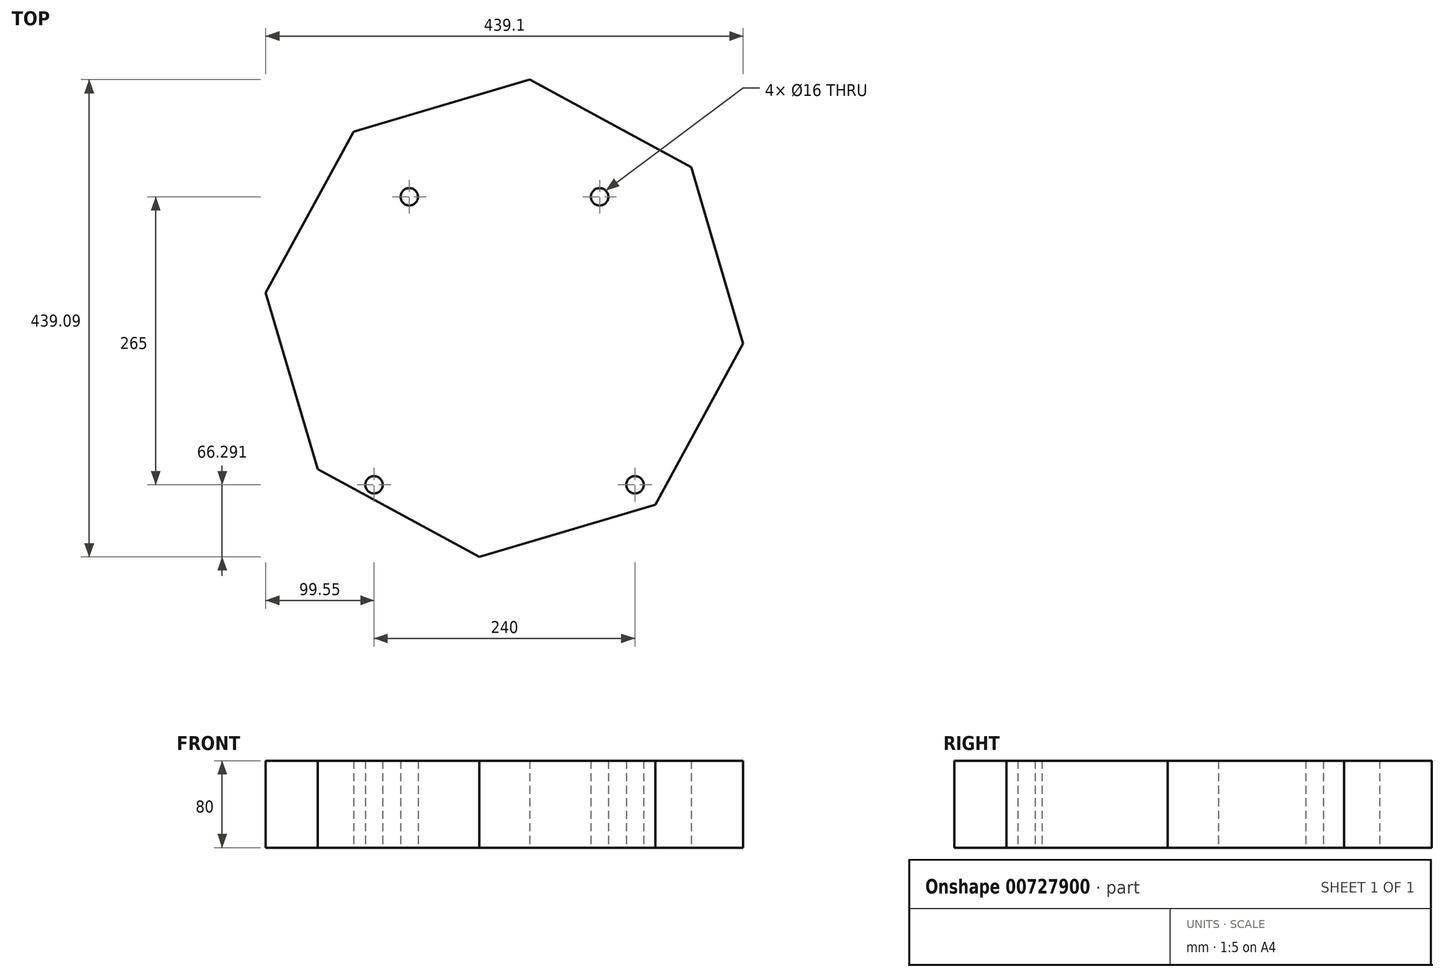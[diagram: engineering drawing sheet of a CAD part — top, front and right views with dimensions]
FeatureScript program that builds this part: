
annotation { "Feature Type Name" : "Feature", "Feature Type Description" : "" }
export const myFeature = defineFeature(function(context is Context, id is Id, definition is map)
    precondition{}
    {
        {
            var Q0;
            Q0=qCreatedBy(makeId("Top.planeOp"),FACE);
            var sketch = newSketch(context, id + "F0", { "sketchPlane" : qUnion([Q0])});
            skLineSegment(sketch, "E0", {"start": v(0, 183.28) * mm, "end": v(0, -81.72) * mm});
            skLineSegment(sketch, "E1", {"start": v(0, -81.72) * mm, "end": v(-120, -81.72) * mm});
            skLineSegment(sketch, "E2", {"start": v(0, -81.72) * mm, "end": v(120, -81.72) * mm});
            skLineSegment(sketch, "E3", {"start": v(0, 183.28) * mm, "end": v(87.5, 183.28) * mm});
            skLineSegment(sketch, "E4", {"start": v(0, 183.28) * mm, "end": v(-87.5, 183.28) * mm});
            skLineSegment(sketch, "E5", {"start": v(-87.5, 183.28) * mm, "end": v(120, -81.72) * mm});
            skLineSegment(sketch, "E6", {"start": v(87.5, 183.28) * mm, "end": v(-120, -81.72) * mm});
            skLineSegment(sketch, "E7", {"start": v(-120, -81.72) * mm, "end": v(-87.5, 183.28) * mm});
            skLineSegment(sketch, "E8", {"start": v(120, -81.72) * mm, "end": v(87.5, 183.28) * mm});
            skCircle(sketch, "E9.cCircle", {"center": v(0, 71.53) * mm, "radius": 203.97 * mm, "construction": true});
            skLineSegment(sketch, "E9.0", {"start": v(-219.55, 94.78) * mm, "end": v(-138.8, 243.21) * mm});
            skLineSegment(sketch, "E9.1", {"start": v(-138.8, 243.21) * mm, "end": v(23.24, 291.08) * mm});
            skLineSegment(sketch, "E9.2", {"start": v(23.24, 291.08) * mm, "end": v(171.68, 210.34) * mm});
            skLineSegment(sketch, "E9.3", {"start": v(171.68, 210.34) * mm, "end": v(219.55, 48.3) * mm});
            skLineSegment(sketch, "E9.4", {"start": v(219.55, 48.3) * mm, "end": v(138.8, -100.14) * mm});
            skLineSegment(sketch, "E9.5", {"start": v(138.8, -100.14) * mm, "end": v(-23.24, -148.01) * mm});
            skLineSegment(sketch, "E9.6", {"start": v(-23.24, -148.01) * mm, "end": v(-171.68, -67.27) * mm});
            skLineSegment(sketch, "E9.7", {"start": v(-171.68, -67.27) * mm, "end": v(-219.55, 94.78) * mm});
            skPoint(sketch, "E9.0.midPoint", {"position": v(-179.18, 169) * mm});
            skCircle(sketch, "E10", {"center": v(-87.5, 183.28) * mm, "radius": 8 * mm});
            skCircle(sketch, "E11", {"center": v(87.5, 183.28) * mm, "radius": 8 * mm});
            skCircle(sketch, "E12", {"center": v(120, -81.72) * mm, "radius": 8 * mm});
            skCircle(sketch, "E13", {"center": v(-120, -81.72) * mm, "radius": 8 * mm});
            skSolve(sketch);
        }
        {
            var Q0;
            Q0=makeQuery(id+"F0.imprint","IMPRINT",FACE,{"disambiguationData":[TD([[makeQuery(id+"F0.imprint","IMPRINT",EDGE,{"derivedFrom":sQuery(id+"F0.wireOp",EDGE,"E9.0")}),-1.0]])]});
            var Q1;
            {var subQ3=sQuery(id+"F0.wireOp",EDGE,"E8");var subQ7=sQuery(id+"F0.wireOp",EDGE,"E12");var subQ8=makeQuery(id+"F0.imprint","INTERSECT",VERTEX,{"derivedFrom":[subQ3,subQ7]});Q1=makeQuery(id+"F0.imprint","IMPRINT",FACE,{"disambiguationData":[TD([[makeQuery(id+"F0.imprint","IMPRINT",EDGE,{"disambiguationData":[TD([[subQ8,-1.0]])],"derivedFrom":subQ3}),1.0]])]});}
            var Q2;
            {var subQ0=sQuery(id+"F0.wireOp",EDGE,"E2");var subQ5=sQuery(id+"F0.wireOp",EDGE,"E12");var subQ6=makeQuery(id+"F0.imprint","INTERSECT",VERTEX,{"derivedFrom":[subQ0,subQ5]});Q2=makeQuery(id+"F0.imprint","IMPRINT",FACE,{"disambiguationData":[TD([[makeQuery(id+"F0.imprint","IMPRINT",EDGE,{"disambiguationData":[TD([[subQ6,1.0]])],"derivedFrom":subQ5}),-1.0]])]});}
            var Q3;
            {var subQ0=sQuery(id+"F0.wireOp",EDGE,"E1");var subQ5=sQuery(id+"F0.wireOp",EDGE,"E13");var subQ7=makeQuery(id+"F0.imprint","INTERSECT",VERTEX,{"derivedFrom":[subQ0,subQ5]});Q3=makeQuery(id+"F0.imprint","IMPRINT",FACE,{"disambiguationData":[TD([[makeQuery(id+"F0.imprint","IMPRINT",EDGE,{"disambiguationData":[TD([[subQ7,-1.0]])],"derivedFrom":subQ5}),-1.0]])]});}
            var Q4;
            {var subQ3=sQuery(id+"F0.wireOp",EDGE,"E7");var subQ7=sQuery(id+"F0.wireOp",EDGE,"E13");var subQ8=makeQuery(id+"F0.imprint","INTERSECT",VERTEX,{"derivedFrom":[subQ3,subQ7]});Q4=makeQuery(id+"F0.imprint","IMPRINT",FACE,{"disambiguationData":[TD([[makeQuery(id+"F0.imprint","IMPRINT",EDGE,{"disambiguationData":[TD([[subQ8,-1.0]])],"derivedFrom":subQ3}),-1.0]])]});}
            var Q5;
            {var subQ0=sQuery(id+"F0.wireOp",EDGE,"E3");var subQ5=sQuery(id+"F0.wireOp",EDGE,"E11");var subQ7=makeQuery(id+"F0.imprint","INTERSECT",VERTEX,{"derivedFrom":[subQ0,subQ5]});Q5=makeQuery(id+"F0.imprint","IMPRINT",FACE,{"disambiguationData":[TD([[makeQuery(id+"F0.imprint","IMPRINT",EDGE,{"disambiguationData":[TD([[subQ7,-1.0]])],"derivedFrom":subQ5}),-1.0]])]});}
            var Q6;
            {var subQ0=sQuery(id+"F0.wireOp",EDGE,"E4");var subQ5=sQuery(id+"F0.wireOp",EDGE,"E10");var subQ6=makeQuery(id+"F0.imprint","INTERSECT",VERTEX,{"derivedFrom":[subQ0,subQ5]});Q6=makeQuery(id+"F0.imprint","IMPRINT",FACE,{"disambiguationData":[TD([[makeQuery(id+"F0.imprint","IMPRINT",EDGE,{"disambiguationData":[TD([[subQ6,1.0]])],"derivedFrom":subQ5}),-1.0]])]});}
            extrude(context, id + "F1", {"entities" : qUnion([Q0, Q1, Q2, Q3, Q4, Q5, Q6]), "depth" : 80 * mm, "offsetDistance" : 25 * mm});
        }
    });
